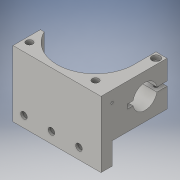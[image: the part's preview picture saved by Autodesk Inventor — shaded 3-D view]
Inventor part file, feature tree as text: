
AUTODESK INVENTOR PART (.ipt)
format: ipt  version: 2016 (Build 200138000, 138)  size: 287,744 bytes
history: native  units: mm
features: sketch x14, projected_geometry x13, extrude x8, hole x6, fillet x1
ambient origin geometry x8: Origin, YZ Plane, XZ Plane, XY Plane, X Axis, Y Axis, Z Axis, Center Point
bodies: Solid1 (feature_tree)
feature tree (42):
  extrude  "Extrusion1"  Depth=40.0mm
  extrude  "Extrusion2"  Depth=57.0mm
  extrude  "Extrusion3"  Depth=70.0mm
  extrude  "Extrusion4"  Depth=22.0mm
  hole  "Hole1"  [1 undecoded]
  extrude  "Extrusion6"  Depth=70.0mm TaperAngle=0.0deg
  fillet  "Fillet1"  Radius=60.0mm
  extrude  "Extrusion7"  Depth=15.0mm
  hole  "Hole4"  [1 undecoded]
  hole  "Hole5"  [1 undecoded]
  hole  "Hole6"  [1 undecoded]
  hole  "Hole7"  [1 undecoded]
  extrude  "Extrusion10"  Depth=10.0mm
  extrude  "Extrusion11"  Depth=10.0mm
  hole  "Hole9"  [1 undecoded]
  sketch  "Sketch1"  dims[d0=20.0mm d1=40.0mm]
  sketch  "Sketch2"  dims[d2=40.0mm d3=57.0mm]
  projected_geometry  "Projected Loop1"
  sketch  "Sketch3"  dims[d4=40.0mm d5=0.0mm d6=70.0mm]
  projected_geometry  "Projected Loop2"
  sketch  "Sketch4"  dims[d7=22.0mm d8=0.0mm d9=22.0mm]
  projected_geometry  "Projected Loop3"
  sketch  "Sketch6"  dims[d10=65.0mm d11=0.0mm d12=16.0mm]
  sketch  "Sketch7"  dims[d13=4.0mm d14=70.0mm d15=0.0mm d19=60.0mm]
  projected_geometry  "Projected Loop5"
  sketch  "Sketch8"  dims[d20=60.0mm]
  projected_geometry  "Projected Loop6"
  sketch  "Sketch13"  dims[d21=6.0mm d22=6.0mm d23=4.0mm d24=2.0mm d25=90.0deg d26=30.0mm d27=20.594885mm d28=15.0mm]
  projected_geometry  "Projected Loop10"
  sketch  "Sketch14"  dims[d29=15.0mm d30=10.0mm d31=0.0mm]
  projected_geometry  "Projected Loop11"
  sketch  "Sketch15"  dims[d32=15.0mm d33=10.0mm]
  sketch  "Sketch16"  dims[d34=20.0mm d35=0.0mm d60=25.0mm]
  projected_geometry  "Projected Loop12"
  projected_geometry  "Projected Loop13"
  sketch  "Sketch18"  dims[d61=25.0mm d62=25.0mm]
  projected_geometry  "Projected Loop15"
  sketch  "Sketch19"  dims[d63=6.0mm d64=6.0mm d65=10.0mm d66=8.0mm d67=90.0deg d68=8.0mm d69=20.594885mm d70=5.0mm]
  projected_geometry  "Projected Loop16"
  sketch  "Sketch20"  dims[d72=4.0mm d73=6.0mm d74=7.5mm d75=4.0mm d76=90.0deg d77=8.0mm d78=20.594885mm d79=3.242mm d80=8.0mm d81=7.5mm d82=4.0mm d83=90.0deg d84=11.8mm d85=20.594885mm d86=10.0mm d87=2.156mm d88=5.69mm d89=7.5mm d90=4.0mm d91=90.0deg d92=8.865mm d93=20.594885mm d104=5.0mm d105=0.0mm d106=5.0mm d107=12.0mm d108=0.0mm d109=2.156mm d110=5.69mm d111=4.0mm d112=2.0mm d113=90.0deg d114=15.0mm d115=20.594885mm]
  projected_geometry  "Projected Loop17"
  projected_geometry  "Projected Loop18"
note: 6 required parameter values undecoded (feature->parameter linkage not recoverable at this tier; creation-order binding heuristic only, values carry confidence <= 0.55)
